# Revit family: PRD_FrankeWS_ClthsHks_StratosDoubleHook_STRX694
name_source: partatom
category: Furniture
revit_build: Autodesk Revit 2018 (Build: 20190510_1515(x64)
units: mm (PartAtom-declared; Revit-internal decimal feet)

## family parameters
Cut with Voids When Loaded = No
Host = Face
OmniClass Number = 23.40.20.21
OmniClass Title = Toilet and Bath Specialties
Room Calculation Point = No
Shared = No

## types (1)
- STRX694
    AssetType = Fixed
    BIMObjectName = PRD_AR_ClothesHooks_StratosDoubleHook_STRX694
    Category = Pr_40_30_78_15, Clothes hooks
    Color = Stainless steel
    Colour = Stainless steel, satin finished
    Default Elevation = 1500 mm  [stored 4.92126 ft]
    Description = Double hook for wall mounting, stainless steel, surface satin finished, 18 mm pipe diameter, drilled hole on bottom for fixation, incl. stainless steel screws and dowels.
    DurationUnit = year
    Features = stainless steel, 18 mm, satin finished, wall mounting, 69x18x60 mm (WxHxD)
    Finish = Satin finished
    Form = Wall mounted
    GrossWeight = 0.15 kg
    HookMaterial = PRD_AR_StainlessSteel_SatinFinished
    IfcExportAs = IfcFurnitureType
    IfcExportType = NOTDEFINED
    IntegralAccessories = Stainless steel screws and dowels incl.
    MainColor = Stainless steel
    Manufacturer = KWC Group AG
    ManufacturerName = KWC Group AG
    ManufacturerURL = www.kwc.com
    Material = Stainless steel
    Model = STRX694
    ModelNumber = 2000057985
    ModelReference = STRX694
    NBSDescription = Clothes hooks
    NBSReference = 45-35-72/322
    Name = STRATOS double hook STRX694
    NetWeight = 0.14 kg
    NominalDepth = 60 mm  [stored 0.19685 ft]
    NominalHeight = 18 mm  [stored 0.0590551 ft]
    NominalLength = 69 mm  [stored 0.226378 ft]
    NominalWidth = 69 mm  [stored 0.226378 ft]
    ProductInformation = https://pim.kwc.com
    Size = 69 x 18 x 60 mm
    Style = Hook
    URL = www.kwc.com
    Uniclass2015Code = Pr_40_30_78_15
    Uniclass2015Title = Clothes hooks
    Uniclass2015Version = Products v1.5
    Version = 1
    WarrantyDurationUnit = year

note: [stored X ft] marks values corroborated as IEEE doubles in the binary element streams (Revit-internal decimal feet)

## geometry (parser evidence)
native form markers: Sweep x3
no freeform markers — native parametric forms only
